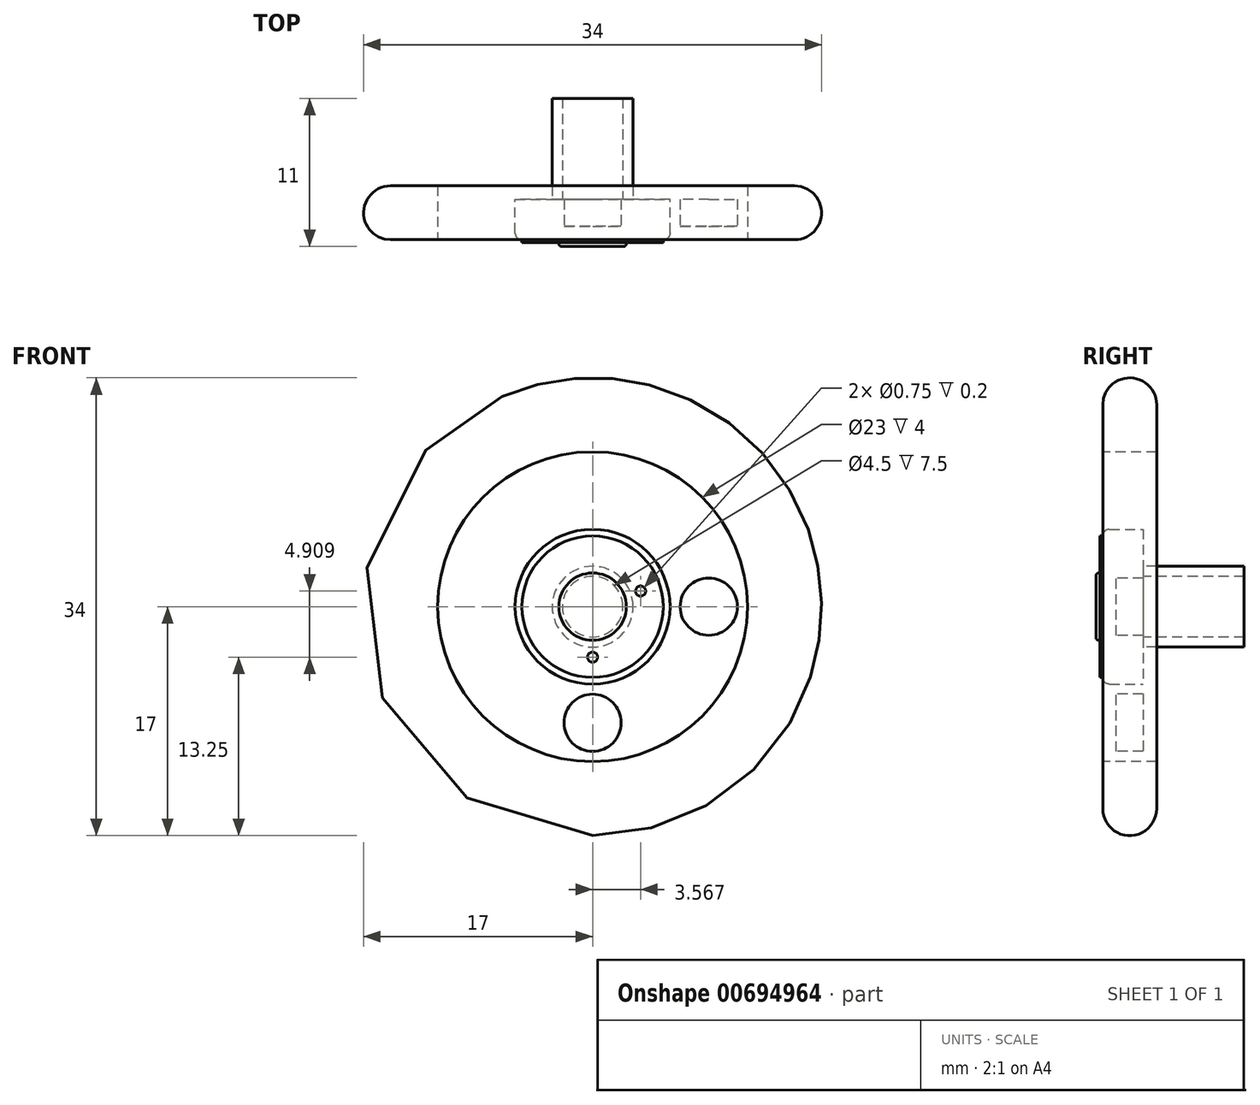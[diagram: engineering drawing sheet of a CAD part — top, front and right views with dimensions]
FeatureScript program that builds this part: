
annotation { "Feature Type Name" : "Feature", "Feature Type Description" : "" }
export const myFeature = defineFeature(function(context is Context, id is Id, definition is map)
    precondition{}
    {
        {
            var Q0;
            Q0=qCreatedBy(makeId("Front.planeOp"),FACE);
            var sketch = newSketch(context, id + "F0", { "sketchPlane" : qUnion([Q0])});
            skCircle(sketch, "E0", {"center": v(0, 0) * mm, "radius": 17 * mm});
            skSolve(sketch);
        }
        {
            var Q0;
            Q0=qSketchRegion(id+"F0",true);
            extrude(context, id + "F1", {"entities" : qUnion([Q0]), "oppositeDirection" : true, "depth" : 4 * mm, "offsetDistance" : 25.4 * mm});
        }
        {
            var Q0;
            Q0=makeQuery(id+"F1.opExtrude","CAP_FACE",FACE,{"disambiguationData":[OSD([sQuery(id+"F0.wireOp",EDGE,"E0")])],"isStart":true});
            var sketch = newSketch(context, id + "F2", { "sketchPlane" : qUnion([Q0])});
            skCircle(sketch, "E1", {"center": v(0, 0) * mm, "radius": 11.5 * mm});
            skSolve(sketch);
        }
        {
            var Q0;
            Q0=qSketchRegion(id+"F2",true);
            extrude(context, id + "F3", {"entities" : qUnion([Q0]), "operationType" : NewBodyOperationType.REMOVE, "oppositeDirection" : true, "depth" : 1 * mm, "offsetDistance" : 25.4 * mm});
        }
        {
            var Q0;
            Q0=makeQuery(id+"F1.opExtrude","CAP_FACE",FACE,{"disambiguationData":[OSD([sQuery(id+"F0.wireOp",EDGE,"E0")])],"isStart":false});
            var sketch = newSketch(context, id + "F4", { "sketchPlane" : qUnion([Q0])});
            skCircle(sketch, "E2", {"center": v(0, 0) * mm, "radius": 11.5 * mm});
            skSolve(sketch);
        }
        {
            var Q0;
            Q0=qSketchRegion(id+"F4",true);
            extrude(context, id + "F5", {"entities" : qUnion([Q0]), "operationType" : NewBodyOperationType.REMOVE, "oppositeDirection" : true, "depth" : 1 * mm, "offsetDistance" : 25.4 * mm});
        }
        {
            var Q0;
            Q0=makeQuery(id+"F1.opExtrude","CAP_EDGE",EDGE,{"disambiguationData":[OSD([sQuery(id+"F0.wireOp",EDGE,"E0")])],"isStart":true});
            fillet(context, id + "F6", {"entities" : qUnion([Q0]), "radius" : 2 * mm, "tangentPropagation" : true, "allowEdgeOverflow" : false});
        }
        {
            var Q0;
            Q0=makeQuery(id+"F1.opExtrude","CAP_EDGE",EDGE,{"disambiguationData":[OSD([sQuery(id+"F0.wireOp",EDGE,"E0")])],"isStart":false});
            fillet(context, id + "F7", {"entities" : qUnion([Q0]), "radius" : 2 * mm, "tangentPropagation" : true, "allowEdgeOverflow" : false});
        }
        {
            var Q0;
            Q0=makeQuery(id+"F3.boolean.opBoolean","COPY",FACE,{"derivedFrom":makeQuery(id+"F3.opExtrude","CAP_FACE",FACE,{"disambiguationData":[OSD([sQuery(id+"F2.wireOp",EDGE,"E1")])],"isStart":false})});
            var sketch = newSketch(context, id + "F8", { "sketchPlane" : qUnion([Q0])});
            skCircle(sketch, "E3", {"center": v(0, 0) * mm, "radius": 2.5 * mm});
            skSolve(sketch);
        }
        {
            var Q0;
            Q0=qSketchRegion(id+"F8",true);
            extrude(context, id + "F9", {"entities" : qUnion([Q0]), "operationType" : NewBodyOperationType.ADD, "depth" : 1.5 * mm, "offsetDistance" : 25.4 * mm});
        }
        {
            var Q0;
            Q0=makeQuery(id+"F3.boolean.opBoolean","COPY",FACE,{"derivedFrom":makeQuery(id+"F3.opExtrude","CAP_FACE",FACE,{"disambiguationData":[OSD([sQuery(id+"F2.wireOp",EDGE,"E1")])],"isStart":false})});
            var sketch = newSketch(context, id + "F10", { "sketchPlane" : qUnion([Q0])});
            skCircle(sketch, "E4", {"center": v(0, 0) * mm, "radius": 5.75 * mm});
            skSolve(sketch);
        }
        {
            var Q0;
            Q0=qSketchRegion(id+"F10",true);
            extrude(context, id + "F11", {"entities" : qUnion([Q0]), "operationType" : NewBodyOperationType.ADD, "depth" : 1 * mm, "offsetDistance" : 25.4 * mm});
        }
        {
            var Q0;
            Q0=makeQuery(id+"F11.opExtrude","CAP_EDGE",EDGE,{"disambiguationData":[OSD([sQuery(id+"F10.wireOp",EDGE,"E4")])],"isStart":false});
            fillet(context, id + "F12", {"entities" : qUnion([Q0]), "radius" : .5 * mm, "tangentPropagation" : true, "allowEdgeOverflow" : false});
        }
        {
            var Q0;
            Q0=makeQuery(id+"F9.opExtrude","CAP_EDGE",EDGE,{"disambiguationData":[OSD([sQuery(id+"F8.wireOp",EDGE,"E3")])],"isStart":false});
            fillet(context, id + "F13", {"entities" : qUnion([Q0]), "radius" : .2 * mm, "tangentPropagation" : true, "allowEdgeOverflow" : false});
        }
        {
            var Q0;
            Q0=makeQuery(id+"F3.boolean.opBoolean","COPY",FACE,{"derivedFrom":makeQuery(id+"F3.opExtrude","CAP_FACE",FACE,{"disambiguationData":[OSD([sQuery(id+"F2.wireOp",EDGE,"E1")])],"isStart":false})});
            var sketch = newSketch(context, id + "F14", { "sketchPlane" : qUnion([Q0])});
            skCircle(sketch, "E5", {"center": v(0, 0) * mm, "radius": 8.62 * mm});
            skCircle(sketch, "E6", {"center": v(0, 8.62) * mm, "radius": 2.12 * mm});
            skCircle(sketch, "E7.1.0", {"center": v(-6.1, 6.1) * mm, "radius": 2.12 * mm});
            skCircle(sketch, "E7.2.0", {"center": v(-8.62, 0) * mm, "radius": 2.12 * mm});
            skCircle(sketch, "E7.3.0", {"center": v(-6.1, -6.1) * mm, "radius": 2.12 * mm});
            skCircle(sketch, "E7.4.0", {"center": v(0, -8.62) * mm, "radius": 2.12 * mm});
            skCircle(sketch, "E7.5.0", {"center": v(6.1, -6.1) * mm, "radius": 2.12 * mm});
            skCircle(sketch, "E7.6.0", {"center": v(8.62, 0) * mm, "radius": 2.12 * mm});
            skCircle(sketch, "E7.7.0", {"center": v(6.1, 6.1) * mm, "radius": 2.12 * mm});
            skSolve(sketch);
        }
        {
            var Q0;
            {var subQ0=sQuery(id+"F14.wireOp",EDGE,"E6");var subQ1=sQuery(id+"F14.wireOp",EDGE,"E5");var subQ2=makeQuery(id+"F14.imprint","INTERSECT",VERTEX,{"disambiguationData":[OD(0.0)],"derivedFrom":[subQ1,subQ0]});Q0=makeQuery(id+"F14.imprint","IMPRINT",FACE,{"disambiguationData":[TD([[makeQuery(id+"F14.imprint","IMPRINT",EDGE,{"disambiguationData":[TD([[subQ2,-1.0]])],"derivedFrom":subQ1}),1.0]])]});}
            var Q1;
            {var subQ0=sQuery(id+"F14.wireOp",EDGE,"E6");var subQ1=sQuery(id+"F14.wireOp",EDGE,"E5");var subQ2=makeQuery(id+"F14.imprint","INTERSECT",VERTEX,{"disambiguationData":[OD(0.0)],"derivedFrom":[subQ1,subQ0]});Q1=makeQuery(id+"F14.imprint","IMPRINT",FACE,{"disambiguationData":[TD([[makeQuery(id+"F14.imprint","IMPRINT",EDGE,{"disambiguationData":[TD([[subQ2,-1.0]])],"derivedFrom":subQ1}),-1.0]])]});}
            var Q2;
            {var subQ0=sQuery(id+"F14.wireOp",EDGE,"E7.1.0");var subQ1=sQuery(id+"F14.wireOp",EDGE,"E5");var subQ2=makeQuery(id+"F14.imprint","INTERSECT",VERTEX,{"disambiguationData":[OD(0.0)],"derivedFrom":[subQ1,subQ0]});Q2=makeQuery(id+"F14.imprint","IMPRINT",FACE,{"disambiguationData":[TD([[makeQuery(id+"F14.imprint","IMPRINT",EDGE,{"disambiguationData":[TD([[subQ2,-1.0]])],"derivedFrom":subQ1}),1.0]])]});}
            var Q3;
            {var subQ0=sQuery(id+"F14.wireOp",EDGE,"E7.1.0");var subQ1=sQuery(id+"F14.wireOp",EDGE,"E5");var subQ2=makeQuery(id+"F14.imprint","INTERSECT",VERTEX,{"disambiguationData":[OD(0.0)],"derivedFrom":[subQ1,subQ0]});Q3=makeQuery(id+"F14.imprint","IMPRINT",FACE,{"disambiguationData":[TD([[makeQuery(id+"F14.imprint","IMPRINT",EDGE,{"disambiguationData":[TD([[subQ2,-1.0]])],"derivedFrom":subQ1}),-1.0]])]});}
            var Q4;
            {var subQ0=sQuery(id+"F14.wireOp",EDGE,"E7.2.0");var subQ1=sQuery(id+"F14.wireOp",EDGE,"E5");var subQ2=makeQuery(id+"F14.imprint","INTERSECT",VERTEX,{"disambiguationData":[OD(0.0)],"derivedFrom":[subQ1,subQ0]});Q4=makeQuery(id+"F14.imprint","IMPRINT",FACE,{"disambiguationData":[TD([[makeQuery(id+"F14.imprint","IMPRINT",EDGE,{"disambiguationData":[TD([[subQ2,-1.0]])],"derivedFrom":subQ1}),1.0]])]});}
            var Q5;
            {var subQ0=sQuery(id+"F14.wireOp",EDGE,"E7.2.0");var subQ1=sQuery(id+"F14.wireOp",EDGE,"E5");var subQ2=makeQuery(id+"F14.imprint","INTERSECT",VERTEX,{"disambiguationData":[OD(0.0)],"derivedFrom":[subQ1,subQ0]});Q5=makeQuery(id+"F14.imprint","IMPRINT",FACE,{"disambiguationData":[TD([[makeQuery(id+"F14.imprint","IMPRINT",EDGE,{"disambiguationData":[TD([[subQ2,-1.0]])],"derivedFrom":subQ1}),-1.0]])]});}
            var Q6;
            {var subQ0=sQuery(id+"F14.wireOp",EDGE,"E7.3.0");var subQ1=sQuery(id+"F14.wireOp",EDGE,"E5");var subQ2=makeQuery(id+"F14.imprint","INTERSECT",VERTEX,{"disambiguationData":[OD(0.0)],"derivedFrom":[subQ1,subQ0]});Q6=makeQuery(id+"F14.imprint","IMPRINT",FACE,{"disambiguationData":[TD([[makeQuery(id+"F14.imprint","IMPRINT",EDGE,{"disambiguationData":[TD([[subQ2,-1.0]])],"derivedFrom":subQ1}),-1.0]])]});}
            var Q7;
            {var subQ0=sQuery(id+"F14.wireOp",EDGE,"E7.3.0");var subQ1=sQuery(id+"F14.wireOp",EDGE,"E5");var subQ2=makeQuery(id+"F14.imprint","INTERSECT",VERTEX,{"disambiguationData":[OD(0.0)],"derivedFrom":[subQ1,subQ0]});Q7=makeQuery(id+"F14.imprint","IMPRINT",FACE,{"disambiguationData":[TD([[makeQuery(id+"F14.imprint","IMPRINT",EDGE,{"disambiguationData":[TD([[subQ2,-1.0]])],"derivedFrom":subQ1}),1.0]])]});}
            var Q8;
            {var subQ0=sQuery(id+"F14.wireOp",EDGE,"E7.4.0");var subQ1=sQuery(id+"F14.wireOp",EDGE,"E5");var subQ2=makeQuery(id+"F14.imprint","INTERSECT",VERTEX,{"disambiguationData":[OD(0.0)],"derivedFrom":[subQ1,subQ0]});Q8=makeQuery(id+"F14.imprint","IMPRINT",FACE,{"disambiguationData":[TD([[makeQuery(id+"F14.imprint","IMPRINT",EDGE,{"disambiguationData":[TD([[subQ2,-1.0]])],"derivedFrom":subQ1}),-1.0]])]});}
            var Q9;
            {var subQ0=sQuery(id+"F14.wireOp",EDGE,"E7.4.0");var subQ1=sQuery(id+"F14.wireOp",EDGE,"E5");var subQ2=makeQuery(id+"F14.imprint","INTERSECT",VERTEX,{"disambiguationData":[OD(0.0)],"derivedFrom":[subQ1,subQ0]});Q9=makeQuery(id+"F14.imprint","IMPRINT",FACE,{"disambiguationData":[TD([[makeQuery(id+"F14.imprint","IMPRINT",EDGE,{"disambiguationData":[TD([[subQ2,-1.0]])],"derivedFrom":subQ1}),1.0]])]});}
            var Q10;
            {var subQ0=sQuery(id+"F14.wireOp",EDGE,"E7.5.0");var subQ1=sQuery(id+"F14.wireOp",EDGE,"E5");var subQ2=makeQuery(id+"F14.imprint","INTERSECT",VERTEX,{"disambiguationData":[OD(0.0)],"derivedFrom":[subQ1,subQ0]});Q10=makeQuery(id+"F14.imprint","IMPRINT",FACE,{"disambiguationData":[TD([[makeQuery(id+"F14.imprint","IMPRINT",EDGE,{"disambiguationData":[TD([[subQ2,-1.0]])],"derivedFrom":subQ1}),-1.0]])]});}
            var Q11;
            {var subQ0=sQuery(id+"F14.wireOp",EDGE,"E7.5.0");var subQ1=sQuery(id+"F14.wireOp",EDGE,"E5");var subQ2=makeQuery(id+"F14.imprint","INTERSECT",VERTEX,{"disambiguationData":[OD(0.0)],"derivedFrom":[subQ1,subQ0]});Q11=makeQuery(id+"F14.imprint","IMPRINT",FACE,{"disambiguationData":[TD([[makeQuery(id+"F14.imprint","IMPRINT",EDGE,{"disambiguationData":[TD([[subQ2,-1.0]])],"derivedFrom":subQ1}),1.0]])]});}
            var Q12;
            {var subQ0=sQuery(id+"F14.wireOp",EDGE,"E7.6.0");var subQ1=sQuery(id+"F14.wireOp",EDGE,"E5");var subQ2=makeQuery(id+"F14.imprint","INTERSECT",VERTEX,{"disambiguationData":[OD(0.0)],"derivedFrom":[subQ1,subQ0]});Q12=makeQuery(id+"F14.imprint","IMPRINT",FACE,{"disambiguationData":[TD([[makeQuery(id+"F14.imprint","IMPRINT",EDGE,{"disambiguationData":[TD([[subQ2,1.0]])],"derivedFrom":subQ1}),1.0]])]});}
            var Q13;
            {var subQ0=sQuery(id+"F14.wireOp",EDGE,"E7.6.0");var subQ1=sQuery(id+"F14.wireOp",EDGE,"E5");var subQ2=makeQuery(id+"F14.imprint","INTERSECT",VERTEX,{"disambiguationData":[OD(0.0)],"derivedFrom":[subQ1,subQ0]});Q13=makeQuery(id+"F14.imprint","IMPRINT",FACE,{"disambiguationData":[TD([[makeQuery(id+"F14.imprint","IMPRINT",EDGE,{"disambiguationData":[TD([[subQ2,1.0]])],"derivedFrom":subQ1}),-1.0]])]});}
            var Q14;
            {var subQ0=sQuery(id+"F14.wireOp",EDGE,"E7.7.0");var subQ1=sQuery(id+"F14.wireOp",EDGE,"E5");var subQ2=makeQuery(id+"F14.imprint","INTERSECT",VERTEX,{"disambiguationData":[OD(0.0)],"derivedFrom":[subQ1,subQ0]});Q14=makeQuery(id+"F14.imprint","IMPRINT",FACE,{"disambiguationData":[TD([[makeQuery(id+"F14.imprint","IMPRINT",EDGE,{"disambiguationData":[TD([[subQ2,-1.0]])],"derivedFrom":subQ1}),-1.0]])]});}
            var Q15;
            {var subQ0=sQuery(id+"F14.wireOp",EDGE,"E7.7.0");var subQ1=sQuery(id+"F14.wireOp",EDGE,"E5");var subQ2=makeQuery(id+"F14.imprint","INTERSECT",VERTEX,{"disambiguationData":[OD(0.0)],"derivedFrom":[subQ1,subQ0]});Q15=makeQuery(id+"F14.imprint","IMPRINT",FACE,{"disambiguationData":[TD([[makeQuery(id+"F14.imprint","IMPRINT",EDGE,{"disambiguationData":[TD([[subQ2,-1.0]])],"derivedFrom":subQ1}),1.0]])]});}
            extrude(context, id + "F15", {"entities" : qUnion([Q0, Q1, Q2, Q3, Q4, Q5, Q6, Q7, Q8, Q9, Q10, Q11, Q12, Q13, Q14, Q15]), "operationType" : NewBodyOperationType.REMOVE, "oppositeDirection" : true, "depth" : 25.4 * mm, "offsetDistance" : 25.4 * mm});
        }
        {
            var Q0;
            Q0=makeQuery(id+"F5.boolean.opBoolean","COPY",FACE,{"derivedFrom":makeQuery(id+"F5.opExtrude","CAP_FACE",FACE,{"disambiguationData":[OSD([sQuery(id+"F4.wireOp",EDGE,"E2")])],"isStart":false})});
            var sketch = newSketch(context, id + "F16", { "sketchPlane" : qUnion([Q0])});
            skCircle(sketch, "E8", {"center": v(0, 0) * mm, "radius": 2.25 * mm});
            skCircle(sketch, "E9", {"center": v(0, 0) * mm, "radius": 3 * mm});
            skSolve(sketch);
        }
        {
            var Q0;
            Q0=qSketchRegion(id+"F16",true);
            extrude(context, id + "F17", {"entities" : qUnion([Q0]), "operationType" : NewBodyOperationType.ADD, "depth" : 7.5 * mm, "offsetDistance" : 25.4 * mm});
        }
        {
            var Q0;
            Q0=makeQuery(id+"F11.opExtrude","CAP_FACE",FACE,{"disambiguationData":[OSD([sQuery(id+"F10.wireOp",EDGE,"E4")])],"isStart":false});
            var sketch = newSketch(context, id + "F18", { "sketchPlane" : qUnion([Q0])});
            skCircle(sketch, "E10", {"center": v(0, 0) * mm, "radius": 3.75 * mm});
            skCircle(sketch, "E11", {"center": v(0, 3.75) * mm, "radius": 0.38 * mm});
            skCircle(sketch, "E12.1.0", {"center": v(-2.2, 3.03) * mm, "radius": 0.38 * mm});
            skCircle(sketch, "E12.2.0", {"center": v(-3.57, 1.16) * mm, "radius": 0.38 * mm});
            skCircle(sketch, "E12.3.0", {"center": v(-3.57, -1.16) * mm, "radius": 0.38 * mm});
            skCircle(sketch, "E12.4.0", {"center": v(-2.2, -3.03) * mm, "radius": 0.38 * mm});
            skCircle(sketch, "E12.5.0", {"center": v(0, -3.75) * mm, "radius": 0.38 * mm});
            skCircle(sketch, "E12.6.0", {"center": v(2.2, -3.03) * mm, "radius": 0.38 * mm});
            skCircle(sketch, "E12.7.0", {"center": v(3.57, -1.16) * mm, "radius": 0.38 * mm});
            skCircle(sketch, "E12.8.0", {"center": v(3.57, 1.16) * mm, "radius": 0.38 * mm});
            skCircle(sketch, "E12.9.0", {"center": v(2.2, 3.03) * mm, "radius": 0.38 * mm});
            skSolve(sketch);
        }
        {
            var Q0;
            {var subQ0=sQuery(id+"F18.wireOp",EDGE,"E12.1.0");var subQ1=sQuery(id+"F18.wireOp",EDGE,"E10");var subQ2=makeQuery(id+"F18.imprint","INTERSECT",VERTEX,{"disambiguationData":[OD(0.0)],"derivedFrom":[subQ1,subQ0]});Q0=makeQuery(id+"F18.imprint","IMPRINT",FACE,{"disambiguationData":[TD([[makeQuery(id+"F18.imprint","IMPRINT",EDGE,{"disambiguationData":[TD([[subQ2,-1.0]])],"derivedFrom":subQ1}),1.0]])]});}
            var Q1;
            {var subQ0=sQuery(id+"F18.wireOp",EDGE,"E12.1.0");var subQ1=sQuery(id+"F18.wireOp",EDGE,"E10");var subQ2=makeQuery(id+"F18.imprint","INTERSECT",VERTEX,{"disambiguationData":[OD(0.0)],"derivedFrom":[subQ1,subQ0]});Q1=makeQuery(id+"F18.imprint","IMPRINT",FACE,{"disambiguationData":[TD([[makeQuery(id+"F18.imprint","IMPRINT",EDGE,{"disambiguationData":[TD([[subQ2,-1.0]])],"derivedFrom":subQ1}),-1.0]])]});}
            var Q2;
            {var subQ0=sQuery(id+"F18.wireOp",EDGE,"E11");var subQ1=sQuery(id+"F18.wireOp",EDGE,"E10");var subQ2=makeQuery(id+"F18.imprint","INTERSECT",VERTEX,{"disambiguationData":[OD(0.0)],"derivedFrom":[subQ1,subQ0]});Q2=makeQuery(id+"F18.imprint","IMPRINT",FACE,{"disambiguationData":[TD([[makeQuery(id+"F18.imprint","IMPRINT",EDGE,{"disambiguationData":[TD([[subQ2,-1.0]])],"derivedFrom":subQ1}),1.0]])]});}
            var Q3;
            {var subQ0=sQuery(id+"F18.wireOp",EDGE,"E11");var subQ1=sQuery(id+"F18.wireOp",EDGE,"E10");var subQ2=makeQuery(id+"F18.imprint","INTERSECT",VERTEX,{"disambiguationData":[OD(0.0)],"derivedFrom":[subQ1,subQ0]});Q3=makeQuery(id+"F18.imprint","IMPRINT",FACE,{"disambiguationData":[TD([[makeQuery(id+"F18.imprint","IMPRINT",EDGE,{"disambiguationData":[TD([[subQ2,-1.0]])],"derivedFrom":subQ1}),-1.0]])]});}
            var Q4;
            {var subQ0=sQuery(id+"F18.wireOp",EDGE,"E12.9.0");var subQ1=sQuery(id+"F18.wireOp",EDGE,"E10");var subQ2=makeQuery(id+"F18.imprint","INTERSECT",VERTEX,{"disambiguationData":[OD(0.0)],"derivedFrom":[subQ1,subQ0]});Q4=makeQuery(id+"F18.imprint","IMPRINT",FACE,{"disambiguationData":[TD([[makeQuery(id+"F18.imprint","IMPRINT",EDGE,{"disambiguationData":[TD([[subQ2,-1.0]])],"derivedFrom":subQ1}),1.0]])]});}
            var Q5;
            {var subQ0=sQuery(id+"F18.wireOp",EDGE,"E12.9.0");var subQ1=sQuery(id+"F18.wireOp",EDGE,"E10");var subQ2=makeQuery(id+"F18.imprint","INTERSECT",VERTEX,{"disambiguationData":[OD(0.0)],"derivedFrom":[subQ1,subQ0]});Q5=makeQuery(id+"F18.imprint","IMPRINT",FACE,{"disambiguationData":[TD([[makeQuery(id+"F18.imprint","IMPRINT",EDGE,{"disambiguationData":[TD([[subQ2,-1.0]])],"derivedFrom":subQ1}),-1.0]])]});}
            var Q6;
            {var subQ0=sQuery(id+"F18.wireOp",EDGE,"E12.8.0");var subQ1=sQuery(id+"F18.wireOp",EDGE,"E10");var subQ2=makeQuery(id+"F18.imprint","INTERSECT",VERTEX,{"disambiguationData":[OD(0.0)],"derivedFrom":[subQ1,subQ0]});Q6=makeQuery(id+"F18.imprint","IMPRINT",FACE,{"disambiguationData":[TD([[makeQuery(id+"F18.imprint","IMPRINT",EDGE,{"disambiguationData":[TD([[subQ2,1.0]])],"derivedFrom":subQ1}),1.0]])]});}
            var Q7;
            {var subQ0=sQuery(id+"F18.wireOp",EDGE,"E12.8.0");var subQ1=sQuery(id+"F18.wireOp",EDGE,"E10");var subQ2=makeQuery(id+"F18.imprint","INTERSECT",VERTEX,{"disambiguationData":[OD(0.0)],"derivedFrom":[subQ1,subQ0]});Q7=makeQuery(id+"F18.imprint","IMPRINT",FACE,{"disambiguationData":[TD([[makeQuery(id+"F18.imprint","IMPRINT",EDGE,{"disambiguationData":[TD([[subQ2,1.0]])],"derivedFrom":subQ1}),-1.0]])]});}
            var Q8;
            {var subQ0=sQuery(id+"F18.wireOp",EDGE,"E12.7.0");var subQ1=sQuery(id+"F18.wireOp",EDGE,"E10");var subQ2=makeQuery(id+"F18.imprint","INTERSECT",VERTEX,{"disambiguationData":[OD(0.0)],"derivedFrom":[subQ1,subQ0]});Q8=makeQuery(id+"F18.imprint","IMPRINT",FACE,{"disambiguationData":[TD([[makeQuery(id+"F18.imprint","IMPRINT",EDGE,{"disambiguationData":[TD([[subQ2,-1.0]])],"derivedFrom":subQ1}),1.0]])]});}
            var Q9;
            {var subQ0=sQuery(id+"F18.wireOp",EDGE,"E12.7.0");var subQ1=sQuery(id+"F18.wireOp",EDGE,"E10");var subQ2=makeQuery(id+"F18.imprint","INTERSECT",VERTEX,{"disambiguationData":[OD(0.0)],"derivedFrom":[subQ1,subQ0]});Q9=makeQuery(id+"F18.imprint","IMPRINT",FACE,{"disambiguationData":[TD([[makeQuery(id+"F18.imprint","IMPRINT",EDGE,{"disambiguationData":[TD([[subQ2,-1.0]])],"derivedFrom":subQ1}),-1.0]])]});}
            var Q10;
            {var subQ0=sQuery(id+"F18.wireOp",EDGE,"E12.6.0");var subQ1=sQuery(id+"F18.wireOp",EDGE,"E10");var subQ2=makeQuery(id+"F18.imprint","INTERSECT",VERTEX,{"disambiguationData":[OD(0.0)],"derivedFrom":[subQ1,subQ0]});Q10=makeQuery(id+"F18.imprint","IMPRINT",FACE,{"disambiguationData":[TD([[makeQuery(id+"F18.imprint","IMPRINT",EDGE,{"disambiguationData":[TD([[subQ2,-1.0]])],"derivedFrom":subQ1}),-1.0]])]});}
            var Q11;
            {var subQ0=sQuery(id+"F18.wireOp",EDGE,"E12.6.0");var subQ1=sQuery(id+"F18.wireOp",EDGE,"E10");var subQ2=makeQuery(id+"F18.imprint","INTERSECT",VERTEX,{"disambiguationData":[OD(0.0)],"derivedFrom":[subQ1,subQ0]});Q11=makeQuery(id+"F18.imprint","IMPRINT",FACE,{"disambiguationData":[TD([[makeQuery(id+"F18.imprint","IMPRINT",EDGE,{"disambiguationData":[TD([[subQ2,-1.0]])],"derivedFrom":subQ1}),1.0]])]});}
            var Q12;
            {var subQ0=sQuery(id+"F18.wireOp",EDGE,"E12.5.0");var subQ1=sQuery(id+"F18.wireOp",EDGE,"E10");var subQ2=makeQuery(id+"F18.imprint","INTERSECT",VERTEX,{"disambiguationData":[OD(0.0)],"derivedFrom":[subQ1,subQ0]});Q12=makeQuery(id+"F18.imprint","IMPRINT",FACE,{"disambiguationData":[TD([[makeQuery(id+"F18.imprint","IMPRINT",EDGE,{"disambiguationData":[TD([[subQ2,-1.0]])],"derivedFrom":subQ1}),-1.0]])]});}
            var Q13;
            {var subQ0=sQuery(id+"F18.wireOp",EDGE,"E12.5.0");var subQ1=sQuery(id+"F18.wireOp",EDGE,"E10");var subQ2=makeQuery(id+"F18.imprint","INTERSECT",VERTEX,{"disambiguationData":[OD(0.0)],"derivedFrom":[subQ1,subQ0]});Q13=makeQuery(id+"F18.imprint","IMPRINT",FACE,{"disambiguationData":[TD([[makeQuery(id+"F18.imprint","IMPRINT",EDGE,{"disambiguationData":[TD([[subQ2,-1.0]])],"derivedFrom":subQ1}),1.0]])]});}
            var Q14;
            {var subQ0=sQuery(id+"F18.wireOp",EDGE,"E12.4.0");var subQ1=sQuery(id+"F18.wireOp",EDGE,"E10");var subQ2=makeQuery(id+"F18.imprint","INTERSECT",VERTEX,{"disambiguationData":[OD(0.0)],"derivedFrom":[subQ1,subQ0]});Q14=makeQuery(id+"F18.imprint","IMPRINT",FACE,{"disambiguationData":[TD([[makeQuery(id+"F18.imprint","IMPRINT",EDGE,{"disambiguationData":[TD([[subQ2,-1.0]])],"derivedFrom":subQ1}),-1.0]])]});}
            var Q15;
            {var subQ0=sQuery(id+"F18.wireOp",EDGE,"E12.4.0");var subQ1=sQuery(id+"F18.wireOp",EDGE,"E10");var subQ2=makeQuery(id+"F18.imprint","INTERSECT",VERTEX,{"disambiguationData":[OD(0.0)],"derivedFrom":[subQ1,subQ0]});Q15=makeQuery(id+"F18.imprint","IMPRINT",FACE,{"disambiguationData":[TD([[makeQuery(id+"F18.imprint","IMPRINT",EDGE,{"disambiguationData":[TD([[subQ2,-1.0]])],"derivedFrom":subQ1}),1.0]])]});}
            var Q16;
            {var subQ0=sQuery(id+"F18.wireOp",EDGE,"E12.3.0");var subQ1=sQuery(id+"F18.wireOp",EDGE,"E10");var subQ2=makeQuery(id+"F18.imprint","INTERSECT",VERTEX,{"disambiguationData":[OD(0.0)],"derivedFrom":[subQ1,subQ0]});Q16=makeQuery(id+"F18.imprint","IMPRINT",FACE,{"disambiguationData":[TD([[makeQuery(id+"F18.imprint","IMPRINT",EDGE,{"disambiguationData":[TD([[subQ2,-1.0]])],"derivedFrom":subQ1}),-1.0]])]});}
            var Q17;
            {var subQ0=sQuery(id+"F18.wireOp",EDGE,"E12.3.0");var subQ1=sQuery(id+"F18.wireOp",EDGE,"E10");var subQ2=makeQuery(id+"F18.imprint","INTERSECT",VERTEX,{"disambiguationData":[OD(0.0)],"derivedFrom":[subQ1,subQ0]});Q17=makeQuery(id+"F18.imprint","IMPRINT",FACE,{"disambiguationData":[TD([[makeQuery(id+"F18.imprint","IMPRINT",EDGE,{"disambiguationData":[TD([[subQ2,-1.0]])],"derivedFrom":subQ1}),1.0]])]});}
            var Q18;
            {var subQ0=sQuery(id+"F18.wireOp",EDGE,"E12.2.0");var subQ1=sQuery(id+"F18.wireOp",EDGE,"E10");var subQ2=makeQuery(id+"F18.imprint","INTERSECT",VERTEX,{"disambiguationData":[OD(0.0)],"derivedFrom":[subQ1,subQ0]});Q18=makeQuery(id+"F18.imprint","IMPRINT",FACE,{"disambiguationData":[TD([[makeQuery(id+"F18.imprint","IMPRINT",EDGE,{"disambiguationData":[TD([[subQ2,-1.0]])],"derivedFrom":subQ1}),-1.0]])]});}
            var Q19;
            {var subQ0=sQuery(id+"F18.wireOp",EDGE,"E12.2.0");var subQ1=sQuery(id+"F18.wireOp",EDGE,"E10");var subQ2=makeQuery(id+"F18.imprint","INTERSECT",VERTEX,{"disambiguationData":[OD(0.0)],"derivedFrom":[subQ1,subQ0]});Q19=makeQuery(id+"F18.imprint","IMPRINT",FACE,{"disambiguationData":[TD([[makeQuery(id+"F18.imprint","IMPRINT",EDGE,{"disambiguationData":[TD([[subQ2,-1.0]])],"derivedFrom":subQ1}),1.0]])]});}
            extrude(context, id + "F19", {"entities" : qUnion([Q0, Q1, Q2, Q3, Q4, Q5, Q6, Q7, Q8, Q9, Q10, Q11, Q12, Q13, Q14, Q15, Q16, Q17, Q18, Q19]), "operationType" : NewBodyOperationType.ADD, "depth" : .2 * mm, "offsetDistance" : 25.4 * mm});
        }
    });
